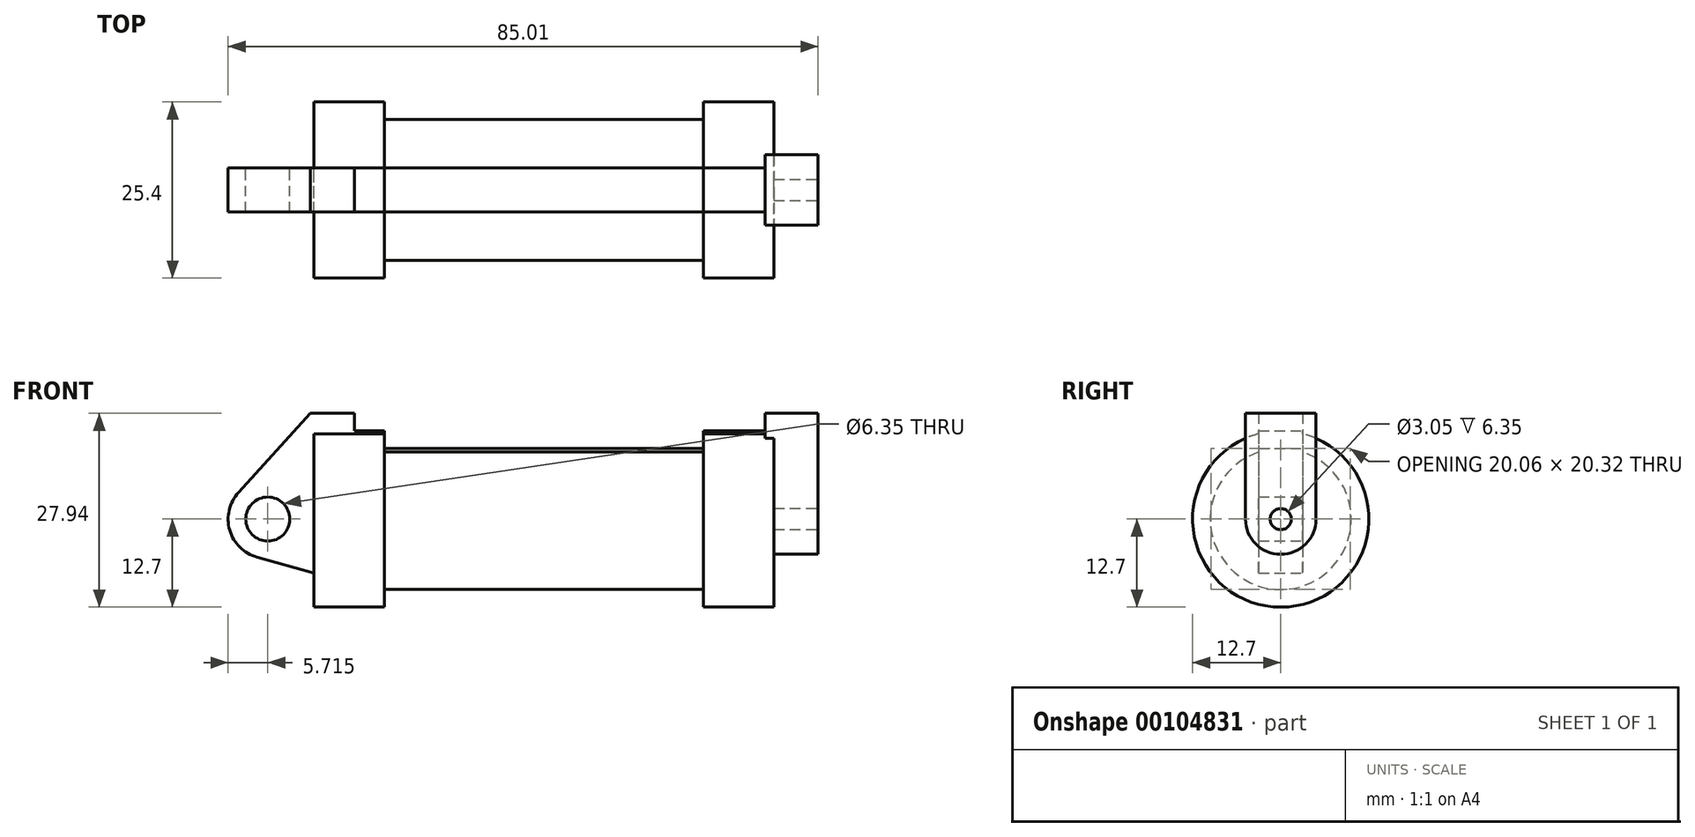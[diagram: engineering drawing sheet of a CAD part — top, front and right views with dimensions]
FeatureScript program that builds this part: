
annotation { "Feature Type Name" : "Feature", "Feature Type Description" : "" }
export const myFeature = defineFeature(function(context is Context, id is Id, definition is map)
    precondition{}
    {
        {
            var Q0;
            Q0=qCreatedBy(makeId("Front.planeOp"),FACE);
            var sketch = newSketch(context, id + "F0", { "sketchPlane" : qUnion([Q0])});
            skLineSegment(sketch, "E0", {"start": v(0, 0) * mm, "end": v(0, 12.7) * mm});
            skLineSegment(sketch, "E1", {"start": v(0, 12.7) * mm, "end": v(10.16, 12.7) * mm});
            skLineSegment(sketch, "E2", {"start": v(10.16, 12.7) * mm, "end": v(10.16, 10.16) * mm});
            skLineSegment(sketch, "E3", {"start": v(10.16, 10.16) * mm, "end": v(56.13, 10.16) * mm});
            skLineSegment(sketch, "E4", {"start": v(56.13, 10.16) * mm, "end": v(56.13, 12.7) * mm});
            skLineSegment(sketch, "E5", {"start": v(56.13, 12.7) * mm, "end": v(66.3, 12.7) * mm});
            skLineSegment(sketch, "E6", {"start": v(66.3, 12.7) * mm, "end": v(66.3, 0) * mm});
            skLineSegment(sketch, "E7", {"start": v(66.3, 0) * mm, "end": v(0, 0) * mm});
            skLineSegment(sketch, "E8", {"start": v(5.84, 15.24) * mm, "end": v(-0.5, 15.24) * mm});
            skLineSegment(sketch, "E9", {"start": v(-0.5, 15.24) * mm, "end": v(-10.88, 3.85) * mm});
            skLineSegment(sketch, "E10", {"start": v(0, 0) * mm, "end": v(-6.65, 0) * mm});
            skCircle(sketch, "E11", {"center": v(-6.65, 0) * mm, "radius": 5.72 * mm});
            skCircle(sketch, "E12", {"center": v(-6.65, 0) * mm, "radius": 3.18 * mm});
            skLineSegment(sketch, "E13", {"start": v(5.84, 15.24) * mm, "end": v(5.84, -9.4) * mm});
            skLineSegment(sketch, "E14", {"start": v(5.84, -9.4) * mm, "end": v(-8.18, -5.5) * mm});
            skSolve(sketch);
        }
        {
            var Q0;
            {var subQ0=sQuery(id+"F0.wireOp",EDGE,"E2");Q0=makeQuery(id+"F0.imprint","IMPRINT",FACE,{"disambiguationData":[TD([[makeQuery(id+"F0.imprint","IMPRINT",EDGE,{"derivedFrom":subQ0}),-1.0]])]});}
            var Q1;
            {var subQ0=sQuery(id+"F0.wireOp",EDGE,"E0");Q1=makeQuery(id+"F0.imprint","IMPRINT",FACE,{"disambiguationData":[TD([[makeQuery(id+"F0.imprint","IMPRINT",EDGE,{"derivedFrom":subQ0}),-1.0]])]});}
            var Q2;
            Q2=sQuery(id+"F0.wireOp",EDGE,"E7");
            revolve(context, id + "F1", {"entities" : qUnion([Q0, Q1]), "axis" : qUnion([Q2]), "revolveType" : RevolveType.FULL});
        }
        {
            var Q0;
            {var subQ0=sQuery(id+"F0.wireOp",EDGE,"E2");Q0=makeQuery(id+"F0.imprint","IMPRINT",FACE,{"disambiguationData":[TD([[makeQuery(id+"F0.imprint","IMPRINT",EDGE,{"derivedFrom":subQ0}),-1.0]])]});}
            var Q1;
            {var subQ0=sQuery(id+"F0.wireOp",EDGE,"E0");Q1=makeQuery(id+"F0.imprint","IMPRINT",FACE,{"disambiguationData":[TD([[makeQuery(id+"F0.imprint","IMPRINT",EDGE,{"derivedFrom":subQ0}),-1.0]])]});}
            var Q2;
            {var subQ3=sQuery(id+"F0.wireOp",EDGE,"E0");Q2=makeQuery(id+"F0.imprint","IMPRINT",FACE,{"disambiguationData":[TD([[makeQuery(id+"F0.imprint","IMPRINT",EDGE,{"derivedFrom":subQ3}),1.0]])]});}
            var Q3;
            {var subQ0=sQuery(id+"F0.wireOp",EDGE,"E14");Q3=makeQuery(id+"F0.imprint","IMPRINT",FACE,{"disambiguationData":[TD([[makeQuery(id+"F0.imprint","IMPRINT",EDGE,{"derivedFrom":subQ0}),-1.0]])]});}
            var Q4;
            {var subQ4=sQuery(id+"F0.wireOp",EDGE,"E12");Q4=makeQuery(id+"F0.imprint","IMPRINT",FACE,{"disambiguationData":[TD([[makeQuery(id+"F0.imprint","IMPRINT",EDGE,{"derivedFrom":subQ4}),-1.0]])]});}
            extrude(context, id + "F2", {"entities" : qUnion([Q0, Q1, Q2, Q3, Q4]), "operationType" : NewBodyOperationType.ADD, "endBound" : BoundingType.SYMMETRIC, "depth" : 6.35 * mm});
        }
        {
            var Q0;
            {var subQ0=sQuery(id+"F0.wireOp",EDGE,"E6");Q0=makeQuery(id+"F2.boolean.opBoolean","MERGE",FACE,{"derivedFrom":[makeQuery(id+"F1.opRevolve","SWEPT_FACE",FACE,{"disambiguationData":[OSD([subQ0])]}),makeQuery(id+"F2.opExtrude","SWEPT_FACE",FACE,{"disambiguationData":[OSD([subQ0])]})]});}
            var sketch = newSketch(context, id + "F3", { "sketchPlane" : qUnion([Q0])});
            skCircle(sketch, "E15", {"center": v(0, 0) * mm, "radius": 1.52 * mm});
            skCircle(sketch, "E16", {"center": v(0, 0) * mm, "radius": 5.08 * mm});
            skLineSegment(sketch, "E17", {"start": v(-5.08, 0) * mm, "end": v(-5.08, 15.24) * mm});
            skLineSegment(sketch, "E18", {"start": v(5.08, 0) * mm, "end": v(5.08, 15.24) * mm});
            skLineSegment(sketch, "E19", {"start": v(-5.08, 15.24) * mm, "end": v(5.08, 15.24) * mm});
            skSolve(sketch);
        }
        {
            var Q0;
            Q0 = qSketchRegion(id + "F3", true);
            extrude(context, id + "F4", {"entities" : qUnion([Q0]), "operationType" : NewBodyOperationType.ADD, "oppositeDirection" : true, "depth" : 1.27 * mm, "hasSecondDirection" : true, "secondDirectionOppositeDirection" : false, "secondDirectionDepth" : 6.35 * mm});
        }
    });
